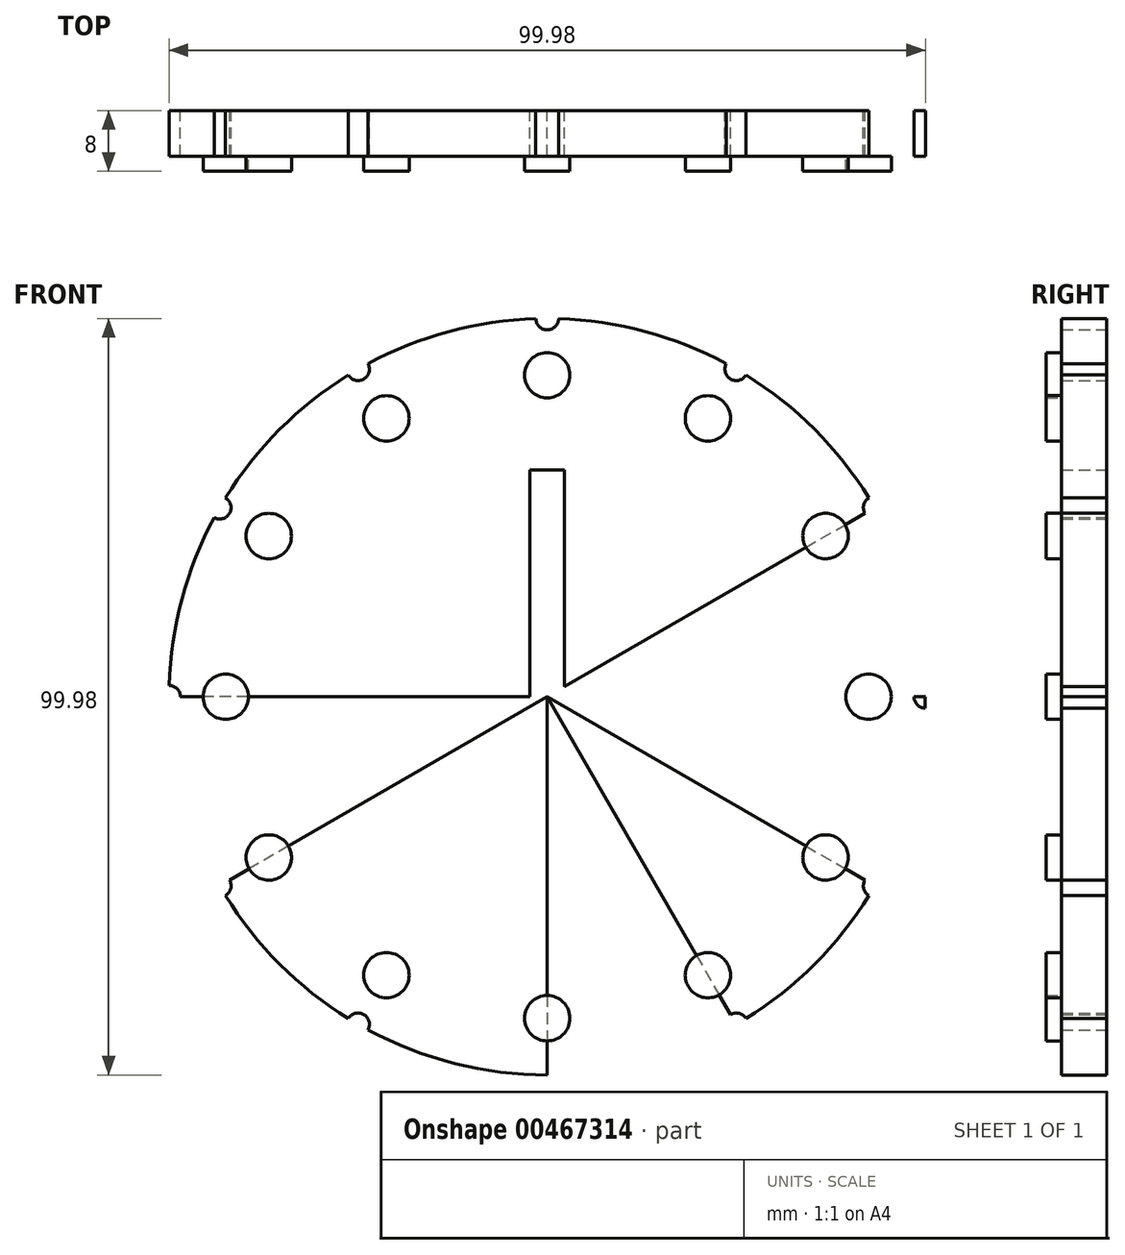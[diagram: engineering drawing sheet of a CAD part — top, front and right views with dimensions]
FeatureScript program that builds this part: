
annotation { "Feature Type Name" : "Feature", "Feature Type Description" : "" }
export const myFeature = defineFeature(function(context is Context, id is Id, definition is map)
    precondition{}
    {
        {
            var Q0;
            Q0=qCreatedBy(makeId("Front.planeOp"),FACE);
            var sketch = newSketch(context, id + "F0", { "sketchPlane" : qUnion([Q0])});
            skCircle(sketch, "E0", {"center": v(0, 0) * mm, "radius": 50 * mm});
            skPoint(sketch, "E1", {"position": v(0, 50) * mm});
            skPoint(sketch, "E2", {"position": v(50, 0) * mm});
            skPoint(sketch, "E3", {"position": v(0, -50) * mm});
            skPoint(sketch, "E4", {"position": v(-50, 0) * mm});
            skPoint(sketch, "E5", {"position": v(-43.3, 25) * mm});
            skPoint(sketch, "E6", {"position": v(-25, 43.3) * mm});
            skPoint(sketch, "E7", {"position": v(25, 43.3) * mm});
            skPoint(sketch, "E8", {"position": v(43.3, 25) * mm});
            skPoint(sketch, "E9", {"position": v(43.3, -25) * mm});
            skPoint(sketch, "E10", {"position": v(25, -43.3) * mm});
            skPoint(sketch, "E11", {"position": v(-25, -43.3) * mm});
            skPoint(sketch, "E12", {"position": v(-43.3, -25) * mm});
            skLineSegment(sketch, "E13", {"start": v(0, 0) * mm, "end": v(0, 50) * mm});
            skLineSegment(sketch, "E14", {"start": v(0, 0) * mm, "end": v(25, 43.3) * mm});
            skLineSegment(sketch, "E15", {"start": v(0, 0) * mm, "end": v(43.3, 25) * mm});
            skLineSegment(sketch, "E16", {"start": v(0, 0) * mm, "end": v(50, 0) * mm});
            skLineSegment(sketch, "E17", {"start": v(0, 0) * mm, "end": v(43.3, -25) * mm});
            skLineSegment(sketch, "E18", {"start": v(0, 0) * mm, "end": v(25, -43.3) * mm});
            skLineSegment(sketch, "E19", {"start": v(0, 0) * mm, "end": v(0, -50) * mm});
            skLineSegment(sketch, "E20", {"start": v(0, 0) * mm, "end": v(-25, -43.3) * mm});
            skLineSegment(sketch, "E21", {"start": v(0, 0) * mm, "end": v(-43.3, -25) * mm});
            skLineSegment(sketch, "E22", {"start": v(0, 0) * mm, "end": v(-50, 0) * mm});
            skLineSegment(sketch, "E23", {"start": v(0, 0) * mm, "end": v(-43.3, 25) * mm});
            skLineSegment(sketch, "E24", {"start": v(0, 0) * mm, "end": v(-25, 43.3) * mm});
            skLineSegment(sketch, "E25.bottom", {"start": v(0, 0) * mm, "end": v(2.3, 0) * mm});
            skLineSegment(sketch, "E25.top", {"start": v(0, 30) * mm, "end": v(2.3, 30) * mm});
            skLineSegment(sketch, "E25.left", {"start": v(0, 0) * mm, "end": v(0, 30) * mm});
            skLineSegment(sketch, "E25.right", {"start": v(2.3, 0) * mm, "end": v(2.3, 30) * mm});
            skLineSegment(sketch, "E26.bottom", {"start": v(0, 0) * mm, "end": v(-2.3, 0) * mm});
            skLineSegment(sketch, "E26.top", {"start": v(0, 30) * mm, "end": v(-2.3, 30) * mm});
            skLineSegment(sketch, "E26.right", {"start": v(-2.3, 0) * mm, "end": v(-2.3, 30) * mm});
            skCircle(sketch, "E27", {"center": v(0, 50) * mm, "radius": 1.5 * mm});
            skCircle(sketch, "E28", {"center": v(25, 43.3) * mm, "radius": 1.5 * mm});
            skCircle(sketch, "E29", {"center": v(43.3, 25) * mm, "radius": 1.5 * mm});
            skCircle(sketch, "E30", {"center": v(50, 0) * mm, "radius": 1.5 * mm});
            skCircle(sketch, "E31", {"center": v(43.3, -25) * mm, "radius": 1.5 * mm});
            skCircle(sketch, "E32", {"center": v(25, -43.3) * mm, "radius": 1.5 * mm});
            skCircle(sketch, "E33", {"center": v(0, -50) * mm, "radius": 1.5 * mm});
            skCircle(sketch, "E34", {"center": v(-25, -43.3) * mm, "radius": 1.5 * mm});
            skCircle(sketch, "E35", {"center": v(-43.3, -25) * mm, "radius": 1.5 * mm});
            skCircle(sketch, "E36", {"center": v(-50, 0) * mm, "radius": 1.5 * mm});
            skCircle(sketch, "E37", {"center": v(-43.3, 25) * mm, "radius": 1.5 * mm});
            skCircle(sketch, "E38", {"center": v(-25, 43.3) * mm, "radius": 1.5 * mm});
            skSolve(sketch);
        }
        {
            var Q0;
            {var subQ3=sQuery(id+"F0.wireOp",EDGE,"E38");var subQ9=sQuery(id+"F0.wireOp",EDGE,"E0");var subQ10=makeQuery(id+"F0.imprint","INTERSECT",VERTEX,{"disambiguationData":[OD(1.0)],"derivedFrom":[subQ9,subQ3]});Q0=makeQuery(id+"F0.imprint","IMPRINT",FACE,{"disambiguationData":[TD([[makeQuery(id+"F0.imprint","IMPRINT",EDGE,{"disambiguationData":[TD([[subQ10,-1.0]])],"derivedFrom":subQ9}),1.0]])]});}
            var Q1;
            {var subQ5=sQuery(id+"F0.wireOp",EDGE,"E26.top");Q1=makeQuery(id+"F0.imprint","IMPRINT",FACE,{"disambiguationData":[TD([[makeQuery(id+"F0.imprint","IMPRINT",EDGE,{"derivedFrom":subQ5}),-1.0]])]});}
            var Q2;
            {var subQ0=sQuery(id+"F0.wireOp",EDGE,"E25.top");Q2=makeQuery(id+"F0.imprint","IMPRINT",FACE,{"disambiguationData":[TD([[makeQuery(id+"F0.imprint","IMPRINT",EDGE,{"derivedFrom":subQ0}),1.0]])]});}
            var Q3;
            {var subQ5=sQuery(id+"F0.wireOp",EDGE,"E29");var subQ9=sQuery(id+"F0.wireOp",EDGE,"E0");var subQ10=makeQuery(id+"F0.imprint","INTERSECT",VERTEX,{"disambiguationData":[OD(1.0)],"derivedFrom":[subQ9,subQ5]});Q3=makeQuery(id+"F0.imprint","IMPRINT",FACE,{"disambiguationData":[TD([[makeQuery(id+"F0.imprint","IMPRINT",EDGE,{"disambiguationData":[TD([[subQ10,-1.0]])],"derivedFrom":subQ9}),1.0]])]});}
            var Q4;
            {var subQ3=sQuery(id+"F0.wireOp",EDGE,"E30");var subQ9=sQuery(id+"F0.wireOp",EDGE,"E0");var subQ10=makeQuery(id+"F0.imprint","INTERSECT",VERTEX,{"disambiguationData":[OD(0.0)],"derivedFrom":[subQ9,subQ3]});Q4=makeQuery(id+"F0.imprint","IMPRINT",FACE,{"disambiguationData":[TD([[makeQuery(id+"F0.imprint","IMPRINT",EDGE,{"disambiguationData":[TD([[subQ10,-1.0]])],"derivedFrom":subQ9}),1.0]])]});}
            var Q5;
            {var subQ0=sQuery(id+"F0.wireOp",EDGE,"E25.bottom");Q5=makeQuery(id+"F0.imprint","IMPRINT",FACE,{"disambiguationData":[TD([[makeQuery(id+"F0.imprint","IMPRINT",EDGE,{"derivedFrom":subQ0}),-1.0]])]});}
            var Q6;
            {var subQ1=sQuery(id+"F0.wireOp",EDGE,"E0");var subQ7=sQuery(id+"F0.wireOp",EDGE,"E32");var subQ9=makeQuery(id+"F0.imprint","INTERSECT",VERTEX,{"disambiguationData":[OD(1.0)],"derivedFrom":[subQ1,subQ7]});Q6=makeQuery(id+"F0.imprint","IMPRINT",FACE,{"disambiguationData":[TD([[makeQuery(id+"F0.imprint","IMPRINT",EDGE,{"disambiguationData":[TD([[subQ9,-1.0]])],"derivedFrom":subQ1}),1.0]])]});}
            var Q7;
            {var subQ1=sQuery(id+"F0.wireOp",EDGE,"E0");var subQ7=sQuery(id+"F0.wireOp",EDGE,"E33");var subQ9=makeQuery(id+"F0.imprint","INTERSECT",VERTEX,{"disambiguationData":[OD(1.0)],"derivedFrom":[subQ1,subQ7]});Q7=makeQuery(id+"F0.imprint","IMPRINT",FACE,{"disambiguationData":[TD([[makeQuery(id+"F0.imprint","IMPRINT",EDGE,{"disambiguationData":[TD([[subQ9,-1.0]])],"derivedFrom":subQ1}),1.0]])]});}
            var Q8;
            {var subQ1=sQuery(id+"F0.wireOp",EDGE,"E0");var subQ7=sQuery(id+"F0.wireOp",EDGE,"E34");var subQ9=makeQuery(id+"F0.imprint","INTERSECT",VERTEX,{"disambiguationData":[OD(1.0)],"derivedFrom":[subQ1,subQ7]});Q8=makeQuery(id+"F0.imprint","IMPRINT",FACE,{"disambiguationData":[TD([[makeQuery(id+"F0.imprint","IMPRINT",EDGE,{"disambiguationData":[TD([[subQ9,-1.0]])],"derivedFrom":subQ1}),1.0]])]});}
            var Q9;
            {var subQ1=sQuery(id+"F0.wireOp",EDGE,"E0");var subQ7=sQuery(id+"F0.wireOp",EDGE,"E35");var subQ9=makeQuery(id+"F0.imprint","INTERSECT",VERTEX,{"disambiguationData":[OD(1.0)],"derivedFrom":[subQ1,subQ7]});Q9=makeQuery(id+"F0.imprint","IMPRINT",FACE,{"disambiguationData":[TD([[makeQuery(id+"F0.imprint","IMPRINT",EDGE,{"disambiguationData":[TD([[subQ9,-1.0]])],"derivedFrom":subQ1}),1.0]])]});}
            var Q10;
            {var subQ0=sQuery(id+"F0.wireOp",EDGE,"E26.bottom");Q10=makeQuery(id+"F0.imprint","IMPRINT",FACE,{"disambiguationData":[TD([[makeQuery(id+"F0.imprint","IMPRINT",EDGE,{"derivedFrom":subQ0}),1.0]])]});}
            var Q11;
            {var subQ5=sQuery(id+"F0.wireOp",EDGE,"E37");var subQ9=sQuery(id+"F0.wireOp",EDGE,"E0");var subQ10=makeQuery(id+"F0.imprint","INTERSECT",VERTEX,{"disambiguationData":[OD(1.0)],"derivedFrom":[subQ9,subQ5]});Q11=makeQuery(id+"F0.imprint","IMPRINT",FACE,{"disambiguationData":[TD([[makeQuery(id+"F0.imprint","IMPRINT",EDGE,{"disambiguationData":[TD([[subQ10,-1.0]])],"derivedFrom":subQ9}),1.0]])]});}
            extrude(context, id + "F1", {"entities" : qUnion([Q0, Q1, Q2, Q3, Q4, Q5, Q6, Q7, Q8, Q9, Q10, Q11]), "depth" : 6 * mm});
        }
        {
            var Q0;
            Q0=makeQuery(id+"F1.opExtrude","CAP_FACE",FACE,{"disambiguationData":[OSD([sQuery(id+"F0.wireOp",EDGE,"E0"),sQuery(id+"F0.wireOp",EDGE,"E25.bottom"),sQuery(id+"F0.wireOp",EDGE,"E25.top"),sQuery(id+"F0.wireOp",EDGE,"E25.right"),sQuery(id+"F0.wireOp",EDGE,"E26.bottom"),sQuery(id+"F0.wireOp",EDGE,"E26.top"),sQuery(id+"F0.wireOp",EDGE,"E26.right"),sQuery(id+"F0.wireOp",EDGE,"E27"),sQuery(id+"F0.wireOp",EDGE,"E28"),sQuery(id+"F0.wireOp",EDGE,"E29"),sQuery(id+"F0.wireOp",EDGE,"E30"),sQuery(id+"F0.wireOp",EDGE,"E31"),sQuery(id+"F0.wireOp",EDGE,"E32"),sQuery(id+"F0.wireOp",EDGE,"E33"),sQuery(id+"F0.wireOp",EDGE,"E34"),sQuery(id+"F0.wireOp",EDGE,"E35"),sQuery(id+"F0.wireOp",EDGE,"E36"),sQuery(id+"F0.wireOp",EDGE,"E37"),sQuery(id+"F0.wireOp",EDGE,"E38")])],"isStart":false});
            var sketch = newSketch(context, id + "F2", { "sketchPlane" : qUnion([Q0])});
            skLineSegment(sketch, "E39", {"start": v(0, 48.5) * mm, "end": v(0, 42.5) * mm});
            skLineSegment(sketch, "E40", {"start": v(24.25, 42) * mm, "end": v(21.25, 36.8) * mm});
            skLineSegment(sketch, "E41", {"start": v(42, 24.25) * mm, "end": v(36.8, 21.25) * mm});
            skLineSegment(sketch, "E42", {"start": v(48.5, 0) * mm, "end": v(42.5, 0) * mm});
            skLineSegment(sketch, "E43", {"start": v(42, -24.25) * mm, "end": v(36.8, -21.25) * mm});
            skLineSegment(sketch, "E44", {"start": v(24.25, -42) * mm, "end": v(21.25, -36.8) * mm});
            skLineSegment(sketch, "E45", {"start": v(0, -48.5) * mm, "end": v(0, -42.5) * mm});
            skLineSegment(sketch, "E46", {"start": v(-24.25, -42) * mm, "end": v(-21.25, -36.8) * mm});
            skLineSegment(sketch, "E47", {"start": v(-42, -24.25) * mm, "end": v(-36.8, -21.25) * mm});
            skLineSegment(sketch, "E48", {"start": v(-48.5, 0) * mm, "end": v(-42.5, 0) * mm});
            skLineSegment(sketch, "E49", {"start": v(-42, 24.25) * mm, "end": v(-36.8, 21.25) * mm});
            skLineSegment(sketch, "E50", {"start": v(-24.25, 42) * mm, "end": v(-21.25, 36.8) * mm});
            skCircle(sketch, "E51", {"center": v(-21.25, 36.8) * mm, "radius": 3 * mm});
            skCircle(sketch, "E52", {"center": v(0, 42.5) * mm, "radius": 3 * mm});
            skCircle(sketch, "E53", {"center": v(-36.8, 21.25) * mm, "radius": 3 * mm});
            skCircle(sketch, "E54", {"center": v(-42.5, 0) * mm, "radius": 3 * mm});
            skCircle(sketch, "E55", {"center": v(-36.8, -21.25) * mm, "radius": 3 * mm});
            skCircle(sketch, "E56", {"center": v(-21.25, -36.8) * mm, "radius": 3 * mm});
            skCircle(sketch, "E57", {"center": v(0, -42.5) * mm, "radius": 3 * mm});
            skCircle(sketch, "E58", {"center": v(21.25, -36.8) * mm, "radius": 3 * mm});
            skCircle(sketch, "E59", {"center": v(36.8, -21.25) * mm, "radius": 3 * mm});
            skCircle(sketch, "E60", {"center": v(42.5, 0) * mm, "radius": 3 * mm});
            skCircle(sketch, "E61", {"center": v(36.8, 21.25) * mm, "radius": 3 * mm});
            skCircle(sketch, "E62", {"center": v(21.25, 36.8) * mm, "radius": 3 * mm});
            skSolve(sketch);
        }
        {
            var Q0;
            Q0=makeQuery(id+"F2.imprint","IMPRINT",FACE,{"disambiguationData":[TD([[makeQuery(id+"F2.imprint","IMPRINT",EDGE,{"derivedFrom":sQuery(id+"F2.wireOp",EDGE,"E52")}),1.0]])]});
            var Q1;
            Q1=makeQuery(id+"F2.imprint","IMPRINT",FACE,{"disambiguationData":[TD([[makeQuery(id+"F2.imprint","IMPRINT",EDGE,{"derivedFrom":sQuery(id+"F2.wireOp",EDGE,"E62")}),1.0]])]});
            var Q2;
            Q2=makeQuery(id+"F2.imprint","IMPRINT",FACE,{"disambiguationData":[TD([[makeQuery(id+"F2.imprint","IMPRINT",EDGE,{"derivedFrom":sQuery(id+"F2.wireOp",EDGE,"E61")}),1.0]])]});
            var Q3;
            Q3=makeQuery(id+"F2.imprint","IMPRINT",FACE,{"disambiguationData":[TD([[makeQuery(id+"F2.imprint","IMPRINT",EDGE,{"derivedFrom":sQuery(id+"F2.wireOp",EDGE,"E60")}),1.0]])]});
            var Q4;
            Q4=makeQuery(id+"F2.imprint","IMPRINT",FACE,{"disambiguationData":[TD([[makeQuery(id+"F2.imprint","IMPRINT",EDGE,{"derivedFrom":sQuery(id+"F2.wireOp",EDGE,"E59")}),1.0]])]});
            var Q5;
            Q5=makeQuery(id+"F2.imprint","IMPRINT",FACE,{"disambiguationData":[TD([[makeQuery(id+"F2.imprint","IMPRINT",EDGE,{"derivedFrom":sQuery(id+"F2.wireOp",EDGE,"E58")}),1.0]])]});
            var Q6;
            Q6=makeQuery(id+"F2.imprint","IMPRINT",FACE,{"disambiguationData":[TD([[makeQuery(id+"F2.imprint","IMPRINT",EDGE,{"derivedFrom":sQuery(id+"F2.wireOp",EDGE,"E57")}),1.0]])]});
            var Q7;
            Q7=makeQuery(id+"F2.imprint","IMPRINT",FACE,{"disambiguationData":[TD([[makeQuery(id+"F2.imprint","IMPRINT",EDGE,{"derivedFrom":sQuery(id+"F2.wireOp",EDGE,"E56")}),1.0]])]});
            var Q8;
            Q8=makeQuery(id+"F2.imprint","IMPRINT",FACE,{"disambiguationData":[TD([[makeQuery(id+"F2.imprint","IMPRINT",EDGE,{"derivedFrom":sQuery(id+"F2.wireOp",EDGE,"E55")}),1.0]])]});
            var Q9;
            Q9=makeQuery(id+"F2.imprint","IMPRINT",FACE,{"disambiguationData":[TD([[makeQuery(id+"F2.imprint","IMPRINT",EDGE,{"derivedFrom":sQuery(id+"F2.wireOp",EDGE,"E54")}),1.0]])]});
            var Q10;
            Q10=makeQuery(id+"F2.imprint","IMPRINT",FACE,{"disambiguationData":[TD([[makeQuery(id+"F2.imprint","IMPRINT",EDGE,{"derivedFrom":sQuery(id+"F2.wireOp",EDGE,"E53")}),1.0]])]});
            var Q11;
            Q11=makeQuery(id+"F2.imprint","IMPRINT",FACE,{"disambiguationData":[TD([[makeQuery(id+"F2.imprint","IMPRINT",EDGE,{"derivedFrom":sQuery(id+"F2.wireOp",EDGE,"E51")}),1.0]])]});
            extrude(context, id + "F3", {"entities" : qUnion([Q0, Q1, Q2, Q3, Q4, Q5, Q6, Q7, Q8, Q9, Q10, Q11]), "operationType" : NewBodyOperationType.ADD, "depth" : 2 * mm});
        }
    });
